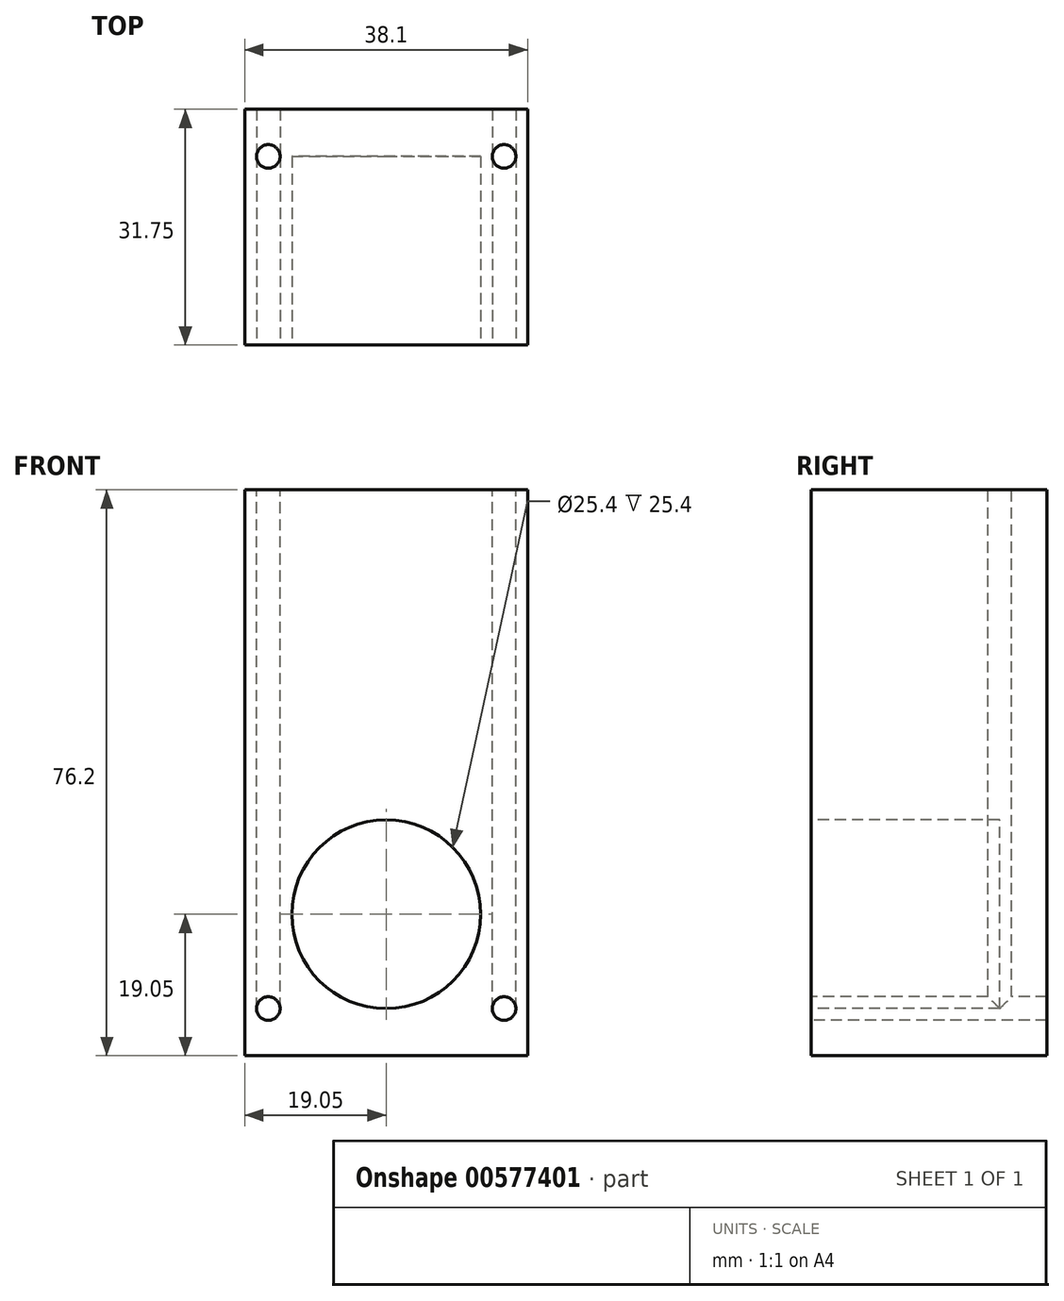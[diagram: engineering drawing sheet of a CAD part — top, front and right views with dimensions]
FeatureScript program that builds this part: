
annotation { "Feature Type Name" : "Feature", "Feature Type Description" : "" }
export const myFeature = defineFeature(function(context is Context, id is Id, definition is map)
    precondition{}
    {
        {
            var Q0;
            Q0=qCreatedBy(makeId("Front.planeOp"),FACE);
            var sketch = newSketch(context, id + "F0", { "sketchPlane" : qUnion([Q0])});
            skLineSegment(sketch, "E0.bottom", {"start": v(19.05, 38.1) * mm, "end": v(-19.05, 38.1) * mm});
            skLineSegment(sketch, "E0.top", {"start": v(19.05, -38.1) * mm, "end": v(-19.05, -38.1) * mm});
            skLineSegment(sketch, "E0.left", {"start": v(19.05, 38.1) * mm, "end": v(19.05, -38.1) * mm});
            skLineSegment(sketch, "E0.right", {"start": v(-19.05, 38.1) * mm, "end": v(-19.05, -38.1) * mm});
            skPoint(sketch, "E0.middle", {"position": v(0, 0) * mm});
            skLineSegment(sketch, "E1", {"start": v(0, -38.1) * mm, "end": v(0, -31.75) * mm});
            skPoint(sketch, "E1.endSnap0", {"position": v(0, -38.1) * mm});
            skLineSegment(sketch, "E2", {"start": v(0, -31.75) * mm, "end": v(0, -19.05) * mm});
            skCircle(sketch, "E3", {"center": v(0, -19.05) * mm, "radius": 12.7 * mm});
            skLineSegment(sketch, "E4", {"start": v(19.05, -38.1) * mm, "end": v(19.05, -31.75) * mm});
            skLineSegment(sketch, "E5", {"start": v(19.05, -31.75) * mm, "end": v(15.87, -31.75) * mm});
            skLineSegment(sketch, "E6", {"start": v(-19.05, -38.1) * mm, "end": v(-19.05, -31.75) * mm});
            skLineSegment(sketch, "E7", {"start": v(-19.05, -31.75) * mm, "end": v(-15.88, -31.75) * mm});
            skCircle(sketch, "E8", {"center": v(-15.88, -31.75) * mm, "radius": 1.59 * mm});
            skCircle(sketch, "E9", {"center": v(15.87, -31.75) * mm, "radius": 1.59 * mm});
            skSolve(sketch);
        }
        {
            var Q0;
            Q0 = qSketchRegion(id + "F0", true);
            var Q1;
            Q1=makeQuery(id+"F0.imprint","IMPRINT",FACE,{"disambiguationData":[TD([[makeQuery(id+"F0.imprint","IMPRINT",EDGE,{"derivedFrom":sQuery(id+"F0.wireOp",EDGE,"E3")}),1.0]])]});
            extrude(context, id + "F1", {"entities" : qUnion([Q0, Q1]), "oppositeDirection" : true, "depth" : 31.75 * mm, "offsetDistance" : 25.4 * mm});
        }
        {
            var Q0;
            Q0=makeQuery(id+"F0.imprint","IMPRINT",FACE,{"disambiguationData":[TD([[makeQuery(id+"F0.imprint","IMPRINT",EDGE,{"derivedFrom":sQuery(id+"F0.wireOp",EDGE,"E3")}),1.0]])]});
            extrude(context, id + "F2", {"entities" : qUnion([Q0]), "operationType" : NewBodyOperationType.REMOVE, "oppositeDirection" : true, "depth" : 25.4 * mm, "offsetDistance" : 25.4 * mm});
        }
        {
            var Q0;
            Q0=makeQuery(id+"F1.opExtrude","SWEPT_FACE",FACE,{"disambiguationData":[OSD([sQuery(id+"F0.wireOp",EDGE,"E0.bottom")])]});
            var sketch = newSketch(context, id + "F3", { "sketchPlane" : qUnion([Q0])});
            skLineSegment(sketch, "E10", {"start": v(-19.05, 31.75) * mm, "end": v(-19.05, 25.4) * mm});
            skLineSegment(sketch, "E11", {"start": v(-19.05, 25.4) * mm, "end": v(-15.88, 25.4) * mm});
            skLineSegment(sketch, "E12", {"start": v(19.05, 31.75) * mm, "end": v(19.05, 25.4) * mm});
            skLineSegment(sketch, "E13", {"start": v(19.05, 25.4) * mm, "end": v(15.87, 25.4) * mm});
            skCircle(sketch, "E14", {"center": v(-15.88, 25.4) * mm, "radius": 1.59 * mm});
            skCircle(sketch, "E15", {"center": v(15.87, 25.4) * mm, "radius": 1.59 * mm});
            skCircle(sketch, "E16", {"center": v(-15.88, 25.4) * mm, "radius": 0.8 * mm});
            skCircle(sketch, "E17", {"center": v(15.87, 25.4) * mm, "radius": 0.8 * mm});
            skSolve(sketch);
        }
        {
            var Q0;
            Q0=makeQuery(id+"F3.imprint","IMPRINT",FACE,{"disambiguationData":[TD([[makeQuery(id+"F3.imprint","IMPRINT",EDGE,{"derivedFrom":sQuery(id+"F3.wireOp",EDGE,"E15")}),1.0]])]});
            var Q1;
            Q1=makeQuery(id+"F3.imprint","IMPRINT",FACE,{"disambiguationData":[TD([[makeQuery(id+"F3.imprint","IMPRINT",EDGE,{"derivedFrom":sQuery(id+"F3.wireOp",EDGE,"E17")}),1.0]])]});
            var Q2;
            Q2=makeQuery(id+"F3.imprint","IMPRINT",FACE,{"disambiguationData":[TD([[makeQuery(id+"F3.imprint","IMPRINT",EDGE,{"derivedFrom":sQuery(id+"F3.wireOp",EDGE,"E14")}),1.0]])]});
            var Q3;
            Q3=makeQuery(id+"F3.imprint","IMPRINT",FACE,{"disambiguationData":[TD([[makeQuery(id+"F3.imprint","IMPRINT",EDGE,{"derivedFrom":sQuery(id+"F3.wireOp",EDGE,"E16")}),1.0]])]});
            extrude(context, id + "F4", {"entities" : qUnion([Q0, Q1, Q2, Q3]), "operationType" : NewBodyOperationType.REMOVE, "oppositeDirection" : true, "depth" : 69.85 * mm, "offsetDistance" : 25.4 * mm});
        }
        {
            var Q0;
            Q0=makeQuery(id+"F3.imprint","IMPRINT",FACE,{"disambiguationData":[TD([[makeQuery(id+"F3.imprint","IMPRINT",EDGE,{"derivedFrom":sQuery(id+"F3.wireOp",EDGE,"E16")}),1.0]])]});
            var Q1;
            Q1=makeQuery(id+"F3.imprint","IMPRINT",FACE,{"disambiguationData":[TD([[makeQuery(id+"F3.imprint","IMPRINT",EDGE,{"derivedFrom":sQuery(id+"F3.wireOp",EDGE,"E17")}),1.0]])]});
            extrude(context, id + "F5", {"entities" : qUnion([Q0, Q1]), "operationType" : NewBodyOperationType.REMOVE, "oppositeDirection" : true, "depth" : 69.85 * mm, "offsetDistance" : 25.4 * mm});
        }
    });
